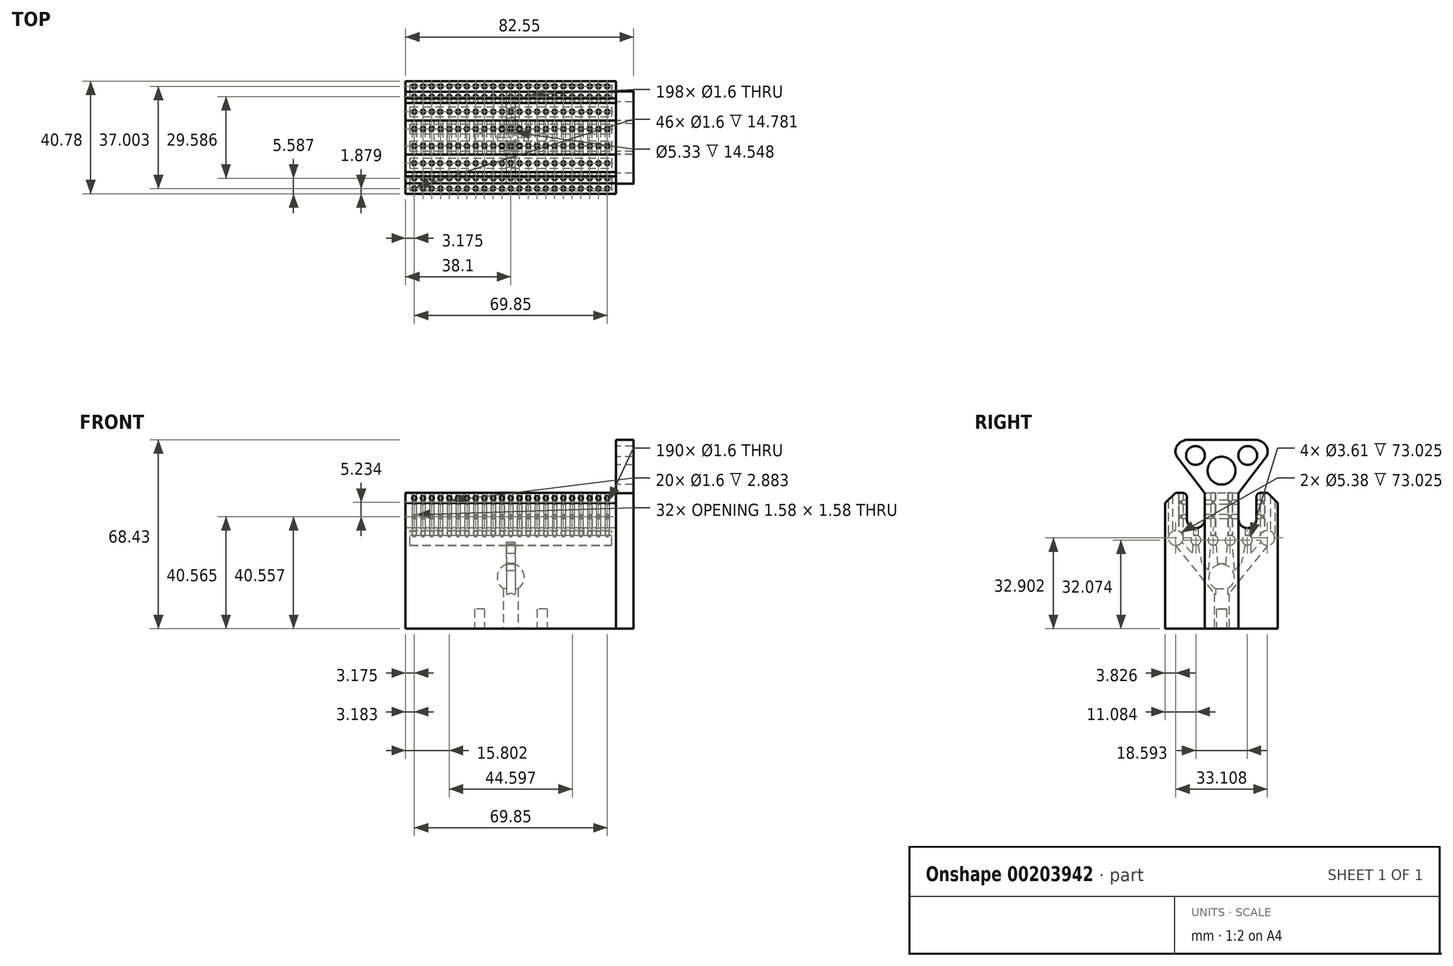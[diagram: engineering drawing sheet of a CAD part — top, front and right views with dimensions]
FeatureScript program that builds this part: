
annotation { "Feature Type Name" : "Feature", "Feature Type Description" : "" }
export const myFeature = defineFeature(function(context is Context, id is Id, definition is map)
    precondition{}
    {
        {
            var Q0;
            Q0=qCreatedBy(makeId("Top.planeOp"),FACE);
            var sketch = newSketch(context, id + "F0", { "sketchPlane" : qUnion([Q0])});
            skPoint(sketch, "E0.middle", {"position": v(0, 0) * mm});
            skCircle(sketch, "E1", {"center": v(-34.92, 18.5) * mm, "radius": 0.8 * mm});
            skCircle(sketch, "E2", {"center": v(-31.75, 18.5) * mm, "radius": 0.8 * mm});
            skCircle(sketch, "E3", {"center": v(-28.58, 18.5) * mm, "radius": 0.8 * mm});
            skCircle(sketch, "E4", {"center": v(-25.4, 18.5) * mm, "radius": 0.8 * mm});
            skCircle(sketch, "E5", {"center": v(-22.23, 18.5) * mm, "radius": 0.8 * mm});
            skCircle(sketch, "E6", {"center": v(-19.05, 18.5) * mm, "radius": 0.8 * mm});
            skCircle(sketch, "E7", {"center": v(-15.88, 18.5) * mm, "radius": 0.8 * mm});
            skCircle(sketch, "E8", {"center": v(-12.7, 18.5) * mm, "radius": 0.8 * mm});
            skCircle(sketch, "E9", {"center": v(-9.53, 18.5) * mm, "radius": 0.8 * mm});
            skCircle(sketch, "E10", {"center": v(-6.35, 18.5) * mm, "radius": 0.8 * mm});
            skCircle(sketch, "E11", {"center": v(-3.18, 18.5) * mm, "radius": 0.8 * mm});
            skCircle(sketch, "E12", {"center": v(-34.92, 9.3) * mm, "radius": 0.8 * mm});
            skCircle(sketch, "E13", {"center": v(-31.75, 9.33) * mm, "radius": 0.8 * mm});
            skCircle(sketch, "E14", {"center": v(-28.58, 9.33) * mm, "radius": 0.8 * mm});
            skCircle(sketch, "E15", {"center": v(-25.58, 9.3) * mm, "radius": 0.8 * mm});
            skCircle(sketch, "E16", {"center": v(-22.23, 9.33) * mm, "radius": 0.8 * mm});
            skCircle(sketch, "E17", {"center": v(-19.05, 9.33) * mm, "radius": 0.8 * mm});
            skCircle(sketch, "E18", {"center": v(-15.88, 9.33) * mm, "radius": 0.8 * mm});
            skCircle(sketch, "E19", {"center": v(-12.7, 9.33) * mm, "radius": 0.8 * mm});
            skCircle(sketch, "E20", {"center": v(-9.53, 9.33) * mm, "radius": 0.8 * mm});
            skCircle(sketch, "E21", {"center": v(-6.35, 9.33) * mm, "radius": 0.8 * mm});
            skCircle(sketch, "E22", {"center": v(-3.18, 9.33) * mm, "radius": 0.8 * mm});
            skCircle(sketch, "E23", {"center": v(0, 9.3) * mm, "radius": 0.8 * mm});
            skCircle(sketch, "E24", {"center": v(-34.92, 3.08) * mm, "radius": 0.8 * mm});
            skCircle(sketch, "E25", {"center": v(-31.75, 3.06) * mm, "radius": 0.8 * mm});
            skCircle(sketch, "E26", {"center": v(-28.62, 3.09) * mm, "radius": 0.8 * mm});
            skCircle(sketch, "E27", {"center": v(-25.4, 3.06) * mm, "radius": 0.8 * mm});
            skCircle(sketch, "E28", {"center": v(-22.23, 3.06) * mm, "radius": 0.8 * mm});
            skCircle(sketch, "E29", {"center": v(-19.05, 3.06) * mm, "radius": 0.8 * mm});
            skCircle(sketch, "E30", {"center": v(-15.88, 3.06) * mm, "radius": 0.8 * mm});
            skCircle(sketch, "E31", {"center": v(-12.7, 3.06) * mm, "radius": 0.8 * mm});
            skCircle(sketch, "E32", {"center": v(-9.53, 3.06) * mm, "radius": 0.8 * mm});
            skCircle(sketch, "E33", {"center": v(-6.35, 3.06) * mm, "radius": 0.8 * mm});
            skCircle(sketch, "E34", {"center": v(-3.18, 3.06) * mm, "radius": 0.88 * mm});
            skCircle(sketch, "E35", {"center": v(0, 3.18) * mm, "radius": 0.8 * mm});
            skCircle(sketch, "E36", {"center": v(-34.92, 14.73) * mm, "radius": 0.8 * mm});
            skCircle(sketch, "E37", {"center": v(-31.75, 14.73) * mm, "radius": 0.8 * mm});
            skCircle(sketch, "E38", {"center": v(-28.58, 14.73) * mm, "radius": 0.8 * mm});
            skCircle(sketch, "E39", {"center": v(-25.4, 14.73) * mm, "radius": 0.8 * mm});
            skCircle(sketch, "E40", {"center": v(-22.23, 14.73) * mm, "radius": 0.8 * mm});
            skCircle(sketch, "E41", {"center": v(-19.05, 14.73) * mm, "radius": 0.8 * mm});
            skCircle(sketch, "E42", {"center": v(-15.88, 14.73) * mm, "radius": 0.8 * mm});
            skCircle(sketch, "E43", {"center": v(-12.7, 14.73) * mm, "radius": 0.8 * mm});
            skCircle(sketch, "E44", {"center": v(-9.53, 14.73) * mm, "radius": 0.8 * mm});
            skCircle(sketch, "E45", {"center": v(-6.28, 14.8) * mm, "radius": 0.8 * mm});
            skCircle(sketch, "E46", {"center": v(-3.18, 14.73) * mm, "radius": 0.8 * mm});
            skCircle(sketch, "E47", {"center": v(0, 14.73) * mm, "radius": 0.8 * mm});
            skCircle(sketch, "E48.MirrorC", {"center": v(0, -3.18) * mm, "radius": 0.8 * mm});
            skCircle(sketch, "E49.MirrorC", {"center": v(-3.18, -3.06) * mm, "radius": 0.88 * mm});
            skCircle(sketch, "E50.MirrorC", {"center": v(-6.35, -3.06) * mm, "radius": 0.8 * mm});
            skCircle(sketch, "E51.MirrorC", {"center": v(-9.53, -3.06) * mm, "radius": 0.8 * mm});
            skCircle(sketch, "E52.MirrorC", {"center": v(-12.7, -3.06) * mm, "radius": 0.8 * mm});
            skCircle(sketch, "E53.MirrorC", {"center": v(-15.88, -3.06) * mm, "radius": 0.8 * mm});
            skCircle(sketch, "E54.MirrorC", {"center": v(-19.05, -3.06) * mm, "radius": 0.8 * mm});
            skCircle(sketch, "E55.MirrorC", {"center": v(-22.23, -3.06) * mm, "radius": 0.8 * mm});
            skCircle(sketch, "E56.MirrorC", {"center": v(-25.4, -3.06) * mm, "radius": 0.8 * mm});
            skCircle(sketch, "E57.MirrorC", {"center": v(-28.62, -3.09) * mm, "radius": 0.8 * mm});
            skCircle(sketch, "E58.MirrorC", {"center": v(-31.75, -3.06) * mm, "radius": 0.8 * mm});
            skCircle(sketch, "E59.MirrorC", {"center": v(-34.92, -3.08) * mm, "radius": 0.8 * mm});
            skCircle(sketch, "E60.MirrorC", {"center": v(-34.92, -9.3) * mm, "radius": 0.8 * mm});
            skCircle(sketch, "E61.MirrorC", {"center": v(-31.75, -9.33) * mm, "radius": 0.8 * mm});
            skCircle(sketch, "E62.MirrorC", {"center": v(-28.58, -9.33) * mm, "radius": 0.8 * mm});
            skCircle(sketch, "E63.MirrorC", {"center": v(-25.58, -9.3) * mm, "radius": 0.8 * mm});
            skCircle(sketch, "E64.MirrorC", {"center": v(-22.23, -9.33) * mm, "radius": 0.8 * mm});
            skCircle(sketch, "E65.MirrorC", {"center": v(-19.05, -9.33) * mm, "radius": 0.8 * mm});
            skCircle(sketch, "E66.MirrorC", {"center": v(-15.88, -9.33) * mm, "radius": 0.8 * mm});
            skCircle(sketch, "E67.MirrorC", {"center": v(-12.7, -9.33) * mm, "radius": 0.8 * mm});
            skCircle(sketch, "E68.MirrorC", {"center": v(-9.53, -9.33) * mm, "radius": 0.8 * mm});
            skCircle(sketch, "E69.MirrorC", {"center": v(-6.35, -9.33) * mm, "radius": 0.8 * mm});
            skCircle(sketch, "E70.MirrorC", {"center": v(-3.18, -9.33) * mm, "radius": 0.8 * mm});
            skCircle(sketch, "E71.MirrorC", {"center": v(0, -9.3) * mm, "radius": 0.8 * mm});
            skCircle(sketch, "E72.MirrorC", {"center": v(0, -18.5) * mm, "radius": 0.8 * mm});
            skCircle(sketch, "E73.MirrorC", {"center": v(-3.18, -14.73) * mm, "radius": 0.8 * mm});
            skCircle(sketch, "E74.MirrorC", {"center": v(-3.18, -18.5) * mm, "radius": 0.8 * mm});
            skCircle(sketch, "E75.MirrorC", {"center": v(-6.35, -18.5) * mm, "radius": 0.8 * mm});
            skCircle(sketch, "E76.MirrorC", {"center": v(-6.28, -14.8) * mm, "radius": 0.8 * mm});
            skCircle(sketch, "E77.MirrorC", {"center": v(-9.53, -14.73) * mm, "radius": 0.8 * mm});
            skCircle(sketch, "E78.MirrorC", {"center": v(-9.53, -18.5) * mm, "radius": 0.8 * mm});
            skCircle(sketch, "E79.MirrorC", {"center": v(-12.7, -14.73) * mm, "radius": 0.8 * mm});
            skCircle(sketch, "E80.MirrorC", {"center": v(-12.7, -18.5) * mm, "radius": 0.8 * mm});
            skCircle(sketch, "E81.MirrorC", {"center": v(-15.88, -14.73) * mm, "radius": 0.8 * mm});
            skCircle(sketch, "E82.MirrorC", {"center": v(-15.88, -18.5) * mm, "radius": 0.8 * mm});
            skCircle(sketch, "E83.MirrorC", {"center": v(-19.05, -18.5) * mm, "radius": 0.8 * mm});
            skCircle(sketch, "E84.MirrorC", {"center": v(-19.05, -14.73) * mm, "radius": 0.8 * mm});
            skCircle(sketch, "E85.MirrorC", {"center": v(-22.23, -14.73) * mm, "radius": 0.8 * mm});
            skCircle(sketch, "E86.MirrorC", {"center": v(-22.23, -18.5) * mm, "radius": 0.8 * mm});
            skCircle(sketch, "E87.MirrorC", {"center": v(-25.4, -18.5) * mm, "radius": 0.8 * mm});
            skCircle(sketch, "E88.MirrorC", {"center": v(-25.4, -14.73) * mm, "radius": 0.8 * mm});
            skCircle(sketch, "E89.MirrorC", {"center": v(-28.58, -14.73) * mm, "radius": 0.8 * mm});
            skCircle(sketch, "E90.MirrorC", {"center": v(-28.58, -18.5) * mm, "radius": 0.8 * mm});
            skCircle(sketch, "E91.MirrorC", {"center": v(-34.92, -14.73) * mm, "radius": 0.8 * mm});
            skCircle(sketch, "E92.MirrorC", {"center": v(-31.75, -14.73) * mm, "radius": 0.8 * mm});
            skCircle(sketch, "E93.MirrorC", {"center": v(-31.75, -18.5) * mm, "radius": 0.8 * mm});
            skCircle(sketch, "E94.MirrorC", {"center": v(-34.92, -18.5) * mm, "radius": 0.8 * mm});
            skCircle(sketch, "E95.MirrorC", {"center": v(6.28, 14.8) * mm, "radius": 0.8 * mm});
            skCircle(sketch, "E96.MirrorC", {"center": v(6.35, 18.5) * mm, "radius": 0.8 * mm});
            skCircle(sketch, "E97.MirrorC", {"center": v(22.23, 18.5) * mm, "radius": 0.8 * mm});
            skCircle(sketch, "E98.MirrorC", {"center": v(31.75, 14.73) * mm, "radius": 0.8 * mm});
            skCircle(sketch, "E99.MirrorC", {"center": v(9.53, 14.73) * mm, "radius": 0.8 * mm});
            skCircle(sketch, "E100.MirrorC", {"center": v(0, 18.5) * mm, "radius": 0.8 * mm});
            skCircle(sketch, "E101.MirrorC", {"center": v(12.7, 18.5) * mm, "radius": 0.8 * mm});
            skCircle(sketch, "E102.MirrorC", {"center": v(3.18, 14.73) * mm, "radius": 0.8 * mm});
            skCircle(sketch, "E103.MirrorC", {"center": v(22.23, 14.73) * mm, "radius": 0.8 * mm});
            skCircle(sketch, "E104.MirrorC", {"center": v(34.92, 18.5) * mm, "radius": 0.8 * mm});
            skCircle(sketch, "E105.MirrorC", {"center": v(19.05, 18.5) * mm, "radius": 0.8 * mm});
            skCircle(sketch, "E106.MirrorC", {"center": v(25.4, 18.5) * mm, "radius": 0.8 * mm});
            skCircle(sketch, "E107.MirrorC", {"center": v(12.7, 14.73) * mm, "radius": 0.8 * mm});
            skCircle(sketch, "E108.MirrorC", {"center": v(15.88, 14.73) * mm, "radius": 0.8 * mm});
            skCircle(sketch, "E109.MirrorC", {"center": v(9.53, 18.5) * mm, "radius": 0.8 * mm});
            skCircle(sketch, "E110.MirrorC", {"center": v(28.58, 18.5) * mm, "radius": 0.8 * mm});
            skCircle(sketch, "E111.MirrorC", {"center": v(3.18, 18.5) * mm, "radius": 0.8 * mm});
            skCircle(sketch, "E112.MirrorC", {"center": v(31.75, 18.5) * mm, "radius": 0.8 * mm});
            skCircle(sketch, "E113.MirrorC", {"center": v(19.05, 14.73) * mm, "radius": 0.8 * mm});
            skCircle(sketch, "E114.MirrorC", {"center": v(15.88, 18.5) * mm, "radius": 0.8 * mm});
            skCircle(sketch, "E115.MirrorC", {"center": v(28.58, 14.73) * mm, "radius": 0.8 * mm});
            skCircle(sketch, "E116.MirrorC", {"center": v(25.4, 14.73) * mm, "radius": 0.8 * mm});
            skCircle(sketch, "E117.MirrorC", {"center": v(22.23, 9.33) * mm, "radius": 0.8 * mm});
            skCircle(sketch, "E118.MirrorC", {"center": v(12.7, 9.33) * mm, "radius": 0.8 * mm});
            skCircle(sketch, "E119.MirrorC", {"center": v(6.35, 9.33) * mm, "radius": 0.8 * mm});
            skCircle(sketch, "E120.MirrorC", {"center": v(28.58, 9.33) * mm, "radius": 0.8 * mm});
            skCircle(sketch, "E121.MirrorC", {"center": v(34.92, 9.3) * mm, "radius": 0.8 * mm});
            skCircle(sketch, "E122.MirrorC", {"center": v(25.58, 9.3) * mm, "radius": 0.8 * mm});
            skCircle(sketch, "E123.MirrorC", {"center": v(15.88, 9.33) * mm, "radius": 0.8 * mm});
            skCircle(sketch, "E124.MirrorC", {"center": v(9.53, 9.33) * mm, "radius": 0.8 * mm});
            skCircle(sketch, "E125.MirrorC", {"center": v(31.75, 9.33) * mm, "radius": 0.8 * mm});
            skCircle(sketch, "E126.MirrorC", {"center": v(19.05, 9.33) * mm, "radius": 0.8 * mm});
            skCircle(sketch, "E127.MirrorC", {"center": v(3.18, 9.33) * mm, "radius": 0.8 * mm});
            skCircle(sketch, "E128.MirrorC", {"center": v(9.53, 3.06) * mm, "radius": 0.8 * mm});
            skCircle(sketch, "E129.MirrorC", {"center": v(12.7, 3.06) * mm, "radius": 0.8 * mm});
            skCircle(sketch, "E130.MirrorC", {"center": v(22.23, 3.06) * mm, "radius": 0.8 * mm});
            skCircle(sketch, "E131.MirrorC", {"center": v(6.35, 3.06) * mm, "radius": 0.8 * mm});
            skCircle(sketch, "E132.MirrorC", {"center": v(31.75, 3.06) * mm, "radius": 0.8 * mm});
            skCircle(sketch, "E133.MirrorC", {"center": v(3.18, 3.06) * mm, "radius": 0.88 * mm});
            skCircle(sketch, "E134.MirrorC", {"center": v(15.88, 3.06) * mm, "radius": 0.8 * mm});
            skCircle(sketch, "E135.MirrorC", {"center": v(19.05, 3.06) * mm, "radius": 0.8 * mm});
            skCircle(sketch, "E136.MirrorC", {"center": v(28.62, 3.09) * mm, "radius": 0.8 * mm});
            skCircle(sketch, "E137.MirrorC", {"center": v(25.4, 3.06) * mm, "radius": 0.8 * mm});
            skCircle(sketch, "E138.MirrorC", {"center": v(34.92, 3.08) * mm, "radius": 0.8 * mm});
            skCircle(sketch, "E139.MirrorC", {"center": v(28.62, -3.09) * mm, "radius": 0.8 * mm});
            skCircle(sketch, "E140.MirrorC", {"center": v(12.7, -3.06) * mm, "radius": 0.8 * mm});
            skCircle(sketch, "E141.MirrorC", {"center": v(34.92, -3.08) * mm, "radius": 0.8 * mm});
            skCircle(sketch, "E142.MirrorC", {"center": v(9.53, -3.06) * mm, "radius": 0.8 * mm});
            skCircle(sketch, "E143.MirrorC", {"center": v(22.23, -3.06) * mm, "radius": 0.8 * mm});
            skCircle(sketch, "E144.MirrorC", {"center": v(31.75, -3.06) * mm, "radius": 0.8 * mm});
            skCircle(sketch, "E145.MirrorC", {"center": v(6.35, -3.06) * mm, "radius": 0.8 * mm});
            skCircle(sketch, "E146.MirrorC", {"center": v(15.88, -3.06) * mm, "radius": 0.8 * mm});
            skCircle(sketch, "E147.MirrorC", {"center": v(19.05, -3.06) * mm, "radius": 0.8 * mm});
            skCircle(sketch, "E148.MirrorC", {"center": v(25.4, -3.06) * mm, "radius": 0.8 * mm});
            skCircle(sketch, "E149.MirrorC", {"center": v(3.18, -3.06) * mm, "radius": 0.88 * mm});
            skCircle(sketch, "E150.MirrorC", {"center": v(12.7, -9.33) * mm, "radius": 0.8 * mm});
            skCircle(sketch, "E151.MirrorC", {"center": v(9.53, -9.33) * mm, "radius": 0.8 * mm});
            skCircle(sketch, "E152.MirrorC", {"center": v(34.92, -9.3) * mm, "radius": 0.8 * mm});
            skCircle(sketch, "E153.MirrorC", {"center": v(6.35, -9.33) * mm, "radius": 0.8 * mm});
            skCircle(sketch, "E154.MirrorC", {"center": v(22.23, -9.33) * mm, "radius": 0.8 * mm});
            skCircle(sketch, "E155.MirrorC", {"center": v(3.18, -9.33) * mm, "radius": 0.8 * mm});
            skCircle(sketch, "E156.MirrorC", {"center": v(28.58, -9.33) * mm, "radius": 0.8 * mm});
            skCircle(sketch, "E157.MirrorC", {"center": v(15.88, -9.33) * mm, "radius": 0.8 * mm});
            skCircle(sketch, "E158.MirrorC", {"center": v(31.75, -9.33) * mm, "radius": 0.8 * mm});
            skCircle(sketch, "E159.MirrorC", {"center": v(19.05, -9.33) * mm, "radius": 0.8 * mm});
            skCircle(sketch, "E160.MirrorC", {"center": v(25.58, -9.3) * mm, "radius": 0.8 * mm});
            skCircle(sketch, "E161.MirrorC", {"center": v(25.4, -18.5) * mm, "radius": 0.8 * mm});
            skCircle(sketch, "E162.MirrorC", {"center": v(0, -14.73) * mm, "radius": 0.8 * mm});
            skCircle(sketch, "E163.MirrorC", {"center": v(6.28, -14.8) * mm, "radius": 0.8 * mm});
            skCircle(sketch, "E164.MirrorC", {"center": v(15.88, -18.5) * mm, "radius": 0.8 * mm});
            skCircle(sketch, "E165.MirrorC", {"center": v(9.53, -18.5) * mm, "radius": 0.8 * mm});
            skCircle(sketch, "E166.MirrorC", {"center": v(34.92, -18.5) * mm, "radius": 0.8 * mm});
            skCircle(sketch, "E167.MirrorC", {"center": v(34.92, -14.73) * mm, "radius": 0.8 * mm});
            skCircle(sketch, "E168.MirrorC", {"center": v(6.35, -18.5) * mm, "radius": 0.8 * mm});
            skCircle(sketch, "E169.MirrorC", {"center": v(12.7, -18.5) * mm, "radius": 0.8 * mm});
            skCircle(sketch, "E170.MirrorC", {"center": v(19.05, -14.73) * mm, "radius": 0.8 * mm});
            skCircle(sketch, "E171.MirrorC", {"center": v(3.18, -14.73) * mm, "radius": 0.8 * mm});
            skCircle(sketch, "E172.MirrorC", {"center": v(31.75, -18.5) * mm, "radius": 0.8 * mm});
            skCircle(sketch, "E173.MirrorC", {"center": v(12.7, -14.73) * mm, "radius": 0.8 * mm});
            skCircle(sketch, "E174.MirrorC", {"center": v(15.88, -14.73) * mm, "radius": 0.8 * mm});
            skCircle(sketch, "E175.MirrorC", {"center": v(31.75, -14.73) * mm, "radius": 0.8 * mm});
            skCircle(sketch, "E176.MirrorC", {"center": v(9.53, -14.73) * mm, "radius": 0.8 * mm});
            skCircle(sketch, "E177.MirrorC", {"center": v(3.18, -18.5) * mm, "radius": 0.8 * mm});
            skCircle(sketch, "E178.MirrorC", {"center": v(22.23, -14.73) * mm, "radius": 0.8 * mm});
            skCircle(sketch, "E179.MirrorC", {"center": v(19.05, -18.5) * mm, "radius": 0.8 * mm});
            skCircle(sketch, "E180.MirrorC", {"center": v(25.4, -14.73) * mm, "radius": 0.8 * mm});
            skCircle(sketch, "E181.MirrorC", {"center": v(28.58, -14.73) * mm, "radius": 0.8 * mm});
            skCircle(sketch, "E182.MirrorC", {"center": v(22.23, -18.5) * mm, "radius": 0.8 * mm});
            skCircle(sketch, "E183.MirrorC", {"center": v(28.58, -18.5) * mm, "radius": 0.8 * mm});
            skCircle(sketch, "E184.MirrorC", {"center": v(34.92, 14.73) * mm, "radius": 0.8 * mm});
            skSolve(sketch);
        }
        {
            var Q0;
            Q0=qCreatedBy(makeId("Right.planeOp"),FACE);
            var sketch = newSketch(context, id + "F1", { "sketchPlane" : qUnion([Q0])});
            skArc(sketch, "E185", {"start": v(6.12, 39.66) * mm, "mid": v(9.33, 36.45) * mm, "end": v(12.55, 39.66) * mm});
            skLineSegment(sketch, "E186", {"start": v(12.55, 39.66) * mm, "end": v(12.55, 47.59) * mm});
            skArc(sketch, "E187", {"start": v(12.55, 47.59) * mm, "mid": v(13, 48.7) * mm, "end": v(14.1, 49.19) * mm});
            skLineSegment(sketch, "E188", {"start": v(14.1, 49.19) * mm, "end": v(16.62, 49.19) * mm});
            skLineSegment(sketch, "E189", {"start": v(20.38, 39.66) * mm, "end": v(20.38, 45.48) * mm});
            skLineSegment(sketch, "E190", {"start": v(16.62, 49.19) * mm, "end": v(20.38, 45.48) * mm});
            skLineSegment(sketch, "E191", {"start": v(6.12, 49.19) * mm, "end": v(6.12, 39.66) * mm});
            skLineSegment(sketch, "E192.MirrorCS", {"start": v(-6.12, 49.19) * mm, "end": v(-6.12, 39.66) * mm});
            skArc(sketch, "E193.MirrorCS", {"start": v(-6.12, 39.66) * mm, "mid": v(-9.33, 36.45) * mm, "end": v(-12.55, 39.66) * mm});
            skLineSegment(sketch, "E194.MirrorCS", {"start": v(-12.55, 39.66) * mm, "end": v(-12.55, 47.59) * mm});
            skArc(sketch, "E195.MirrorCS", {"start": v(-12.55, 47.59) * mm, "mid": v(-13, 48.7) * mm, "end": v(-14.1, 49.19) * mm});
            skLineSegment(sketch, "E196.MirrorCS", {"start": v(-14.1, 49.19) * mm, "end": v(-16.62, 49.19) * mm});
            skLineSegment(sketch, "E197.MirrorCS", {"start": v(-16.62, 49.19) * mm, "end": v(-20.38, 45.48) * mm});
            skLineSegment(sketch, "E198.MirrorCS", {"start": v(-20.38, 39.66) * mm, "end": v(-20.38, 45.48) * mm});
            skLineSegment(sketch, "E199", {"start": v(-20.38, 39.66) * mm, "end": v(-20.38, 0) * mm});
            skLineSegment(sketch, "E200", {"start": v(20.4, 0) * mm, "end": v(20.38, 39.66) * mm});
            skLineSegment(sketch, "E201", {"start": v(-6.12, 49.19) * mm, "end": v(6.12, 49.19) * mm});
            skLineSegment(sketch, "E202", {"start": v(-20.38, 0) * mm, "end": v(20.4, 0) * mm});
            skSolve(sketch);
        }
        {
            var Q0;
            Q0=qCreatedBy(makeId("Right.planeOp"),FACE);
            var sketch = newSketch(context, id + "F2", { "sketchPlane" : qUnion([Q0])});
            skLineSegment(sketch, "E203", {"start": v(0, 0) * mm, "end": v(-6.13, 0) * mm});
            skLineSegment(sketch, "E204", {"start": v(-6.13, 0) * mm, "end": v(-6.13, 49.13) * mm});
            skLineSegment(sketch, "E205", {"start": v(-6.13, 49.13) * mm, "end": v(-17.04, 63.34) * mm});
            skLineSegment(sketch, "E206", {"start": v(-17.04, 63.34) * mm, "end": v(-17.04, 68.43) * mm});
            skLineSegment(sketch, "E207.MirrorCS", {"start": v(0, 0) * mm, "end": v(6.13, 0) * mm});
            skLineSegment(sketch, "E208.MirrorCS", {"start": v(6.13, 0) * mm, "end": v(6.13, 49.13) * mm});
            skLineSegment(sketch, "E209.MirrorCS", {"start": v(6.13, 49.13) * mm, "end": v(17.04, 63.34) * mm});
            skLineSegment(sketch, "E210.MirrorCS", {"start": v(17.04, 63.34) * mm, "end": v(17.04, 68.43) * mm});
            skLineSegment(sketch, "E211", {"start": v(-17.04, 68.43) * mm, "end": v(17.04, 68.43) * mm});
            skCircle(sketch, "E212", {"center": v(0, 57.25) * mm, "radius": 5.04 * mm});
            skCircle(sketch, "E213", {"center": v(9.44, 62.75) * mm, "radius": 3.4 * mm});
            skCircle(sketch, "E214.MirrorC", {"center": v(-9.44, 62.75) * mm, "radius": 3.4 * mm});
            skSolve(sketch);
        }
        {
            var Q0;
            Q0=qCreatedBy(makeId("Front.planeOp"),FACE);
            var sketch = newSketch(context, id + "F3", { "sketchPlane" : qUnion([Q0])});
            skCircle(sketch, "E215", {"center": v(-34.93, 45.8) * mm, "radius": 0.8 * mm});
            skCircle(sketch, "E216", {"center": v(-31.75, 45.8) * mm, "radius": 0.8 * mm});
            skCircle(sketch, "E217", {"center": v(-28.58, 45.8) * mm, "radius": 0.8 * mm});
            skCircle(sketch, "E218", {"center": v(-25.4, 45.8) * mm, "radius": 0.8 * mm});
            skCircle(sketch, "E219", {"center": v(-22.3, 45.8) * mm, "radius": 0.8 * mm});
            skCircle(sketch, "E220", {"center": v(-19.05, 45.8) * mm, "radius": 0.8 * mm});
            skCircle(sketch, "E221", {"center": v(-15.79, 45.8) * mm, "radius": 0.8 * mm});
            skCircle(sketch, "E222", {"center": v(-12.7, 45.8) * mm, "radius": 0.8 * mm});
            skCircle(sketch, "E223", {"center": v(-6.35, 45.8) * mm, "radius": 0.8 * mm});
            skCircle(sketch, "E224", {"center": v(-9.53, 45.8) * mm, "radius": 0.8 * mm});
            skCircle(sketch, "E225", {"center": v(-3.18, 45.8) * mm, "radius": 0.8 * mm});
            skCircle(sketch, "E226", {"center": v(0, 45.8) * mm, "radius": 0.8 * mm});
            skCircle(sketch, "E227", {"center": v(0, 40.56) * mm, "radius": 0.8 * mm});
            skCircle(sketch, "E228", {"center": v(-3.18, 40.56) * mm, "radius": 0.8 * mm});
            skCircle(sketch, "E229", {"center": v(-6.35, 40.56) * mm, "radius": 0.8 * mm});
            skCircle(sketch, "E230", {"center": v(-9.53, 40.56) * mm, "radius": 0.8 * mm});
            skCircle(sketch, "E231", {"center": v(-12.7, 40.56) * mm, "radius": 0.8 * mm});
            skCircle(sketch, "E232", {"center": v(-15.79, 40.56) * mm, "radius": 0.8 * mm});
            skCircle(sketch, "E233", {"center": v(-19.05, 40.56) * mm, "radius": 0.8 * mm});
            skCircle(sketch, "E234", {"center": v(-22.23, 40.56) * mm, "radius": 0.8 * mm});
            skCircle(sketch, "E235", {"center": v(-25.4, 40.56) * mm, "radius": 0.8 * mm});
            skCircle(sketch, "E236", {"center": v(-28.58, 40.56) * mm, "radius": 0.8 * mm});
            skCircle(sketch, "E237", {"center": v(-31.75, 40.56) * mm, "radius": 0.8 * mm});
            skCircle(sketch, "E238", {"center": v(-34.93, 40.56) * mm, "radius": 0.8 * mm});
            skCircle(sketch, "E239.MirrorC", {"center": v(22.23, 40.56) * mm, "radius": 0.8 * mm});
            skCircle(sketch, "E240.MirrorC", {"center": v(19.05, 40.56) * mm, "radius": 0.8 * mm});
            skCircle(sketch, "E241.MirrorC", {"center": v(25.4, 40.56) * mm, "radius": 0.8 * mm});
            skCircle(sketch, "E242.MirrorC", {"center": v(9.53, 45.8) * mm, "radius": 0.8 * mm});
            skCircle(sketch, "E243.MirrorC", {"center": v(6.35, 45.8) * mm, "radius": 0.8 * mm});
            skCircle(sketch, "E244.MirrorC", {"center": v(3.18, 45.8) * mm, "radius": 0.8 * mm});
            skCircle(sketch, "E245.MirrorC", {"center": v(31.75, 40.56) * mm, "radius": 0.8 * mm});
            skCircle(sketch, "E246.MirrorC", {"center": v(12.7, 40.56) * mm, "radius": 0.8 * mm});
            skCircle(sketch, "E247.MirrorC", {"center": v(34.93, 45.8) * mm, "radius": 0.8 * mm});
            skCircle(sketch, "E248.MirrorC", {"center": v(3.18, 40.56) * mm, "radius": 0.8 * mm});
            skCircle(sketch, "E249.MirrorC", {"center": v(19.05, 45.8) * mm, "radius": 0.8 * mm});
            skCircle(sketch, "E250.MirrorC", {"center": v(25.4, 45.8) * mm, "radius": 0.8 * mm});
            skCircle(sketch, "E251.MirrorC", {"center": v(6.35, 40.56) * mm, "radius": 0.8 * mm});
            skCircle(sketch, "E252.MirrorC", {"center": v(34.93, 40.56) * mm, "radius": 0.8 * mm});
            skCircle(sketch, "E253.MirrorC", {"center": v(15.79, 40.56) * mm, "radius": 0.8 * mm});
            skCircle(sketch, "E254.MirrorC", {"center": v(15.79, 45.8) * mm, "radius": 0.8 * mm});
            skCircle(sketch, "E255.MirrorC", {"center": v(12.7, 45.8) * mm, "radius": 0.8 * mm});
            skCircle(sketch, "E256.MirrorC", {"center": v(22.3, 45.8) * mm, "radius": 0.8 * mm});
            skCircle(sketch, "E257.MirrorC", {"center": v(31.75, 45.8) * mm, "radius": 0.8 * mm});
            skCircle(sketch, "E258.MirrorC", {"center": v(28.58, 45.8) * mm, "radius": 0.8 * mm});
            skCircle(sketch, "E259.MirrorC", {"center": v(9.53, 40.56) * mm, "radius": 0.8 * mm});
            skCircle(sketch, "E260.MirrorC", {"center": v(28.58, 40.56) * mm, "radius": 0.8 * mm});
            skSolve(sketch);
        }
        {
            var Q0;
            Q0=qCreatedBy(makeId("Right.planeOp"),FACE);
            var sketch = newSketch(context, id + "F4", { "sketchPlane" : qUnion([Q0])});
            skCircle(sketch, "E261", {"center": v(-9.3, 32.07) * mm, "radius": 1.8 * mm});
            skCircle(sketch, "E262", {"center": v(-16.55, 32.9) * mm, "radius": 2.7 * mm});
            skCircle(sketch, "E263.MirrorC", {"center": v(16.55, 32.9) * mm, "radius": 2.7 * mm});
            skCircle(sketch, "E264", {"center": v(-3.07, 32.07) * mm, "radius": 1.8 * mm});
            skCircle(sketch, "E265.MirrorC", {"center": v(3.07, 32.07) * mm, "radius": 1.8 * mm});
            skCircle(sketch, "E266.MirrorC", {"center": v(9.3, 32.07) * mm, "radius": 1.8 * mm});
            skSolve(sketch);
        }
        {
            var Q0;
            Q0=qCreatedBy(makeId("Top.planeOp"),FACE);
            var sketch = newSketch(context, id + "F5", { "sketchPlane" : qUnion([Q0])});
            skCircle(sketch, "E267", {"center": v(0, 0) * mm, "radius": 2.67 * mm});
            skCircle(sketch, "E268", {"center": v(-11.3, 0) * mm, "radius": 1.83 * mm});
            skCircle(sketch, "E269", {"center": v(11.3, 0) * mm, "radius": 1.83 * mm});
            skSolve(sketch);
        }
        {
            var Q0;
            Q0=qCreatedBy(makeId("Right.planeOp"),FACE);
            var sketch = newSketch(context, id + "F6", { "sketchPlane" : qUnion([Q0])});
            skLineSegment(sketch, "E270", {"start": v(0, 18.65) * mm, "end": v(7.4, 18.65) * mm});
            skLineSegment(sketch, "E271", {"start": v(7.4, 18.65) * mm, "end": v(0, 18.65) * mm});
            skLineSegment(sketch, "E272", {"start": v(-7.68, 18.65) * mm, "end": v(0, 18.65) * mm});
            skArc(sketch, "E273", {"start": v(4.9, 18.65) * mm, "mid": v(0, 23.55) * mm, "end": v(-4.9, 18.65) * mm});
            skLineSegment(sketch, "E274", {"start": v(-7.68, 18.65) * mm, "end": v(7.4, 18.65) * mm});
            skSolve(sketch);
        }
        {
            var Q0;
            Q0=qCreatedBy(makeId("Right.planeOp"),FACE);
            var sketch = newSketch(context, id + "F7", { "sketchPlane" : qUnion([Q0])});
            skLineSegment(sketch, "E275", {"start": v(-2.1, 32) * mm, "end": v(-1.47, 23.24) * mm});
            skLineSegment(sketch, "E276", {"start": v(-16.53, 32) * mm, "end": v(-14.93, 32) * mm});
            skLineSegment(sketch, "E277", {"start": v(-16.53, 32) * mm, "end": v(-18.13, 32) * mm});
            skLineSegment(sketch, "E278", {"start": v(-10.57, 32) * mm, "end": v(-10.57, 27.36) * mm});
            skLineSegment(sketch, "E279", {"start": v(-8.83, 32) * mm, "end": v(-7.18, 23.76) * mm});
            skLineSegment(sketch, "E280", {"start": v(-4.7, 21.13) * mm, "end": v(-7.18, 23.76) * mm});
            skLineSegment(sketch, "E281", {"start": v(-18.13, 32) * mm, "end": v(-2.45, 12.5) * mm});
            skLineSegment(sketch, "E282", {"start": v(-4.7, 21.13) * mm, "end": v(-3.83, 32) * mm});
            skLineSegment(sketch, "E283", {"start": v(-10.57, 32) * mm, "end": v(-8.83, 32) * mm});
            skLineSegment(sketch, "E284.trimOffspring", {"start": v(-3.83, 32) * mm, "end": v(-2.1, 32) * mm});
            skLineSegment(sketch, "E285.trimOffspring", {"start": v(-10.57, 27.36) * mm, "end": v(-14.93, 32) * mm});
            skLineSegment(sketch, "E286", {"start": v(-1.47, 23.24) * mm, "end": v(0, 23.24) * mm});
            skLineSegment(sketch, "E287", {"start": v(-2.45, 12.5) * mm, "end": v(0, 12.5) * mm});
            skLineSegment(sketch, "E288.MirrorCS", {"start": v(10.57, 27.36) * mm, "end": v(14.93, 32) * mm});
            skLineSegment(sketch, "E289.MirrorCS", {"start": v(8.83, 32) * mm, "end": v(7.18, 23.76) * mm});
            skLineSegment(sketch, "E290.MirrorCS", {"start": v(4.7, 21.13) * mm, "end": v(3.83, 32) * mm});
            skLineSegment(sketch, "E291.MirrorCS", {"start": v(4.7, 21.13) * mm, "end": v(7.18, 23.76) * mm});
            skLineSegment(sketch, "E292.MirrorCS", {"start": v(2.1, 32) * mm, "end": v(1.47, 23.24) * mm});
            skLineSegment(sketch, "E293.MirrorCS", {"start": v(2.45, 12.5) * mm, "end": v(0, 12.5) * mm});
            skLineSegment(sketch, "E294.MirrorCS", {"start": v(16.53, 32) * mm, "end": v(18.13, 32) * mm});
            skLineSegment(sketch, "E295.MirrorCS", {"start": v(1.47, 23.24) * mm, "end": v(0, 23.24) * mm});
            skLineSegment(sketch, "E296.MirrorCS", {"start": v(16.53, 32) * mm, "end": v(14.93, 32) * mm});
            skLineSegment(sketch, "E297.MirrorCS", {"start": v(3.83, 32) * mm, "end": v(2.1, 32) * mm});
            skLineSegment(sketch, "E298.MirrorCS", {"start": v(18.13, 32) * mm, "end": v(2.45, 12.5) * mm});
            skLineSegment(sketch, "E299.MirrorCS", {"start": v(10.57, 32) * mm, "end": v(10.57, 27.36) * mm});
            skLineSegment(sketch, "E300.MirrorCS", {"start": v(10.57, 32) * mm, "end": v(8.83, 32) * mm});
            skSolve(sketch);
        }
        {
            var Q0;
            Q0=makeQuery(id+"F1.imprint","IMPRINT",FACE,{"disambiguationData":[TD([[makeQuery(id+"F1.imprint","IMPRINT",EDGE,{"derivedFrom":sQuery(id+"F1.wireOp",EDGE,"E185")}),-1.0]])]});
            extrude(context, id + "F8", {"entities" : qUnion([Q0]), "endBound" : BoundingType.SYMMETRIC, "depth" : 76.2 * mm});
        }
        {
            var Q0;
            Q0 = qSketchRegion(id + "F4", true);
            extrude(context, id + "F9", {"entities" : qUnion([Q0]), "operationType" : NewBodyOperationType.REMOVE, "endBound" : BoundingType.SYMMETRIC, "oppositeDirection" : true, "depth" : 73.02 * mm});
        }
        {
            var Q0;
            Q0 = qSketchRegion(id + "F0", true);
            var Q1;
            Q1=makeQuery(id+"F8.opExtrude","SWEPT_FACE",FACE,{"disambiguationData":[OSD([sQuery(id+"F1.wireOp",EDGE,"E201")])]});
            extrude(context, id + "F10", {"entities" : qUnion([Q0]), "operationType" : NewBodyOperationType.REMOVE, "endBound" : BoundingType.THROUGH_ALL, "endBoundEntityFace" : qUnion([Q1]), "depth" : 49.19 * mm, "hasSecondDirection" : true, "secondDirectionOppositeDirection" : false, "secondDirectionDepth" : 33.35 * mm});
        }
        {
            var Q0;
            Q0 = qSketchRegion(id + "F2", true);
            var Q1;
            Q1=makeQuery(id+"F8.opExtrude","CAP_FACE",FACE,{"disambiguationData":[OSD([sQuery(id+"F1.wireOp",EDGE,"E185"),sQuery(id+"F1.wireOp",EDGE,"E186"),sQuery(id+"F1.wireOp",EDGE,"E187"),sQuery(id+"F1.wireOp",EDGE,"E188"),sQuery(id+"F1.wireOp",EDGE,"E189"),sQuery(id+"F1.wireOp",EDGE,"E190"),sQuery(id+"F1.wireOp",EDGE,"E191"),sQuery(id+"F1.wireOp",EDGE,"E192.MirrorCS"),sQuery(id+"F1.wireOp",EDGE,"E193.MirrorCS"),sQuery(id+"F1.wireOp",EDGE,"E194.MirrorCS"),sQuery(id+"F1.wireOp",EDGE,"E195.MirrorCS"),sQuery(id+"F1.wireOp",EDGE,"E196.MirrorCS"),sQuery(id+"F1.wireOp",EDGE,"E197.MirrorCS"),sQuery(id+"F1.wireOp",EDGE,"E198.MirrorCS"),sQuery(id+"F1.wireOp",EDGE,"E199"),sQuery(id+"F1.wireOp",EDGE,"E200"),sQuery(id+"F1.wireOp",EDGE,"E201"),sQuery(id+"F1.wireOp",EDGE,"E202")])],"isStart":false});
            extrude(context, id + "F11", {"entities" : qUnion([Q0]), "operationType" : NewBodyOperationType.ADD, "depth" : 44.45 * mm, "hasSecondDirection" : true, "secondDirectionOppositeDirection" : false, "secondDirectionBoundEntityFace" : qUnion([Q1]), "secondDirectionDepth" : 38.1 * mm});
        }
        {
            var Q0;
            Q0 = qSketchRegion(id + "F3", true);
            extrude(context, id + "F12", {"entities" : qUnion([Q0]), "operationType" : NewBodyOperationType.REMOVE, "endBound" : BoundingType.SYMMETRIC, "oppositeDirection" : true, "depth" : 30.86 * mm});
        }
        {
            var Q0;
            Q0=makeQuery(id+"F5.imprint","IMPRINT",FACE,{"disambiguationData":[TD([[makeQuery(id+"F5.imprint","IMPRINT",EDGE,{"derivedFrom":sQuery(id+"F5.wireOp",EDGE,"E268")}),1.0]])]});
            var Q1;
            Q1=makeQuery(id+"F5.imprint","IMPRINT",FACE,{"disambiguationData":[TD([[makeQuery(id+"F5.imprint","IMPRINT",EDGE,{"derivedFrom":sQuery(id+"F5.wireOp",EDGE,"E269")}),1.0]])]});
            var Q2;
            Q2=sQuery(id+"F5.wireOp",EDGE,"E269");
            var Q3;
            Q3=sQuery(id+"F5.wireOp",EDGE,"E268");
            extrude(context, id + "F13", {"entities" : qUnion([Q0, Q1]), "operationType" : NewBodyOperationType.REMOVE, "surfaceEntities" : qUnion([Q2, Q3]), "depth" : 7.11 * mm});
        }
        {
            var Q0;
            Q0=makeQuery(id+"F5.imprint","IMPRINT",FACE,{"disambiguationData":[TD([[makeQuery(id+"F5.imprint","IMPRINT",EDGE,{"derivedFrom":sQuery(id+"F5.wireOp",EDGE,"E267")}),1.0]])]});
            var Q1;
            Q1=sQuery(id+"F5.wireOp",EDGE,"E267");
            extrude(context, id + "F14", {"entities" : qUnion([Q0]), "operationType" : NewBodyOperationType.REMOVE, "surfaceEntities" : qUnion([Q1]), "depth" : 19.94 * mm});
        }
        {
            var Q0;
            {var subQ0=sQuery(id+"F6.wireOp",EDGE,"E273");Q0=makeQuery(id+"F6.imprint","IMPRINT",FACE,{"disambiguationData":[TD([[makeQuery(id+"F6.imprint","IMPRINT",EDGE,{"derivedFrom":subQ0}),1.0]])]});}
            var Q1;
            Q1=sQuery(id+"F6.wireOp",EDGE,"E274");
            revolve(context, id + "F15", {"operationType" : NewBodyOperationType.REMOVE, "entities" : qUnion([Q0]), "axis" : qUnion([Q1]), "revolveType" : RevolveType.FULL, "oppositeDirection" : true});
        }
        {
            var Q0;
            Q0 = qSketchRegion(id + "F7", true);
            extrude(context, id + "F16", {"entities" : qUnion([Q0]), "operationType" : NewBodyOperationType.REMOVE, "endBound" : BoundingType.SYMMETRIC, "oppositeDirection" : true, "depth" : 3.17 * mm});
        }
        {
            var Q0;
            Q0=makeQuery(id+"F11.opExtrude","SWEPT_EDGE",EDGE,{"disambiguationData":[OSD([sQuery(id+"F2.wireOp",EDGE,"E210.MirrorCS"),sQuery(id+"F2.wireOp",EDGE,"E211")])]});
            var Q1;
            Q1=makeQuery(id+"F11.opExtrude","SWEPT_EDGE",EDGE,{"disambiguationData":[OSD([sQuery(id+"F2.wireOp",EDGE,"E206"),sQuery(id+"F2.wireOp",EDGE,"E211")])]});
            var Q2;
            Q2=makeQuery(id+"F11.opExtrude","SWEPT_EDGE",EDGE,{"disambiguationData":[OSD([sQuery(id+"F2.wireOp",EDGE,"E209.MirrorCS"),sQuery(id+"F2.wireOp",EDGE,"E210.MirrorCS")])]});
            var Q3;
            Q3=makeQuery(id+"F11.opExtrude","SWEPT_EDGE",EDGE,{"disambiguationData":[OSD([sQuery(id+"F2.wireOp",EDGE,"E205"),sQuery(id+"F2.wireOp",EDGE,"E206")])]});
            fillet(context, id + "F17", {"entities" : qUnion([Q0, Q1, Q2, Q3]), "radius" : 5.08 * mm, "tangentPropagation" : true, "allowEdgeOverflow" : false});
        }
        {
            var Q0;
            {var subQ0=sQuery(id+"F2.wireOp",EDGE,"E210.MirrorCS");Q0=makeQuery(id+"F17.opFillet","BLEND_EDGE",EDGE,{"blendedFrom":[makeQuery(id+"F11.opExtrude","SWEPT_EDGE",EDGE,{"disambiguationData":[OSD([sQuery(id+"F2.wireOp",EDGE,"E209.MirrorCS"),subQ0])]}),makeQuery(id+"F11.opExtrude","SWEPT_EDGE",EDGE,{"disambiguationData":[OSD([subQ0,sQuery(id+"F2.wireOp",EDGE,"E211")])]})],"blendedInto":[]});}
            fillet(context, id + "F18", {"entities" : qUnion([Q0]), "radius" : 3.8 * mm, "tangentPropagation" : true, "allowEdgeOverflow" : false});
        }
        {
            var Q0;
            {var subQ0=sQuery(id+"F2.wireOp",EDGE,"E206");Q0=makeQuery(id+"F17.opFillet","BLEND_EDGE",EDGE,{"blendedFrom":[makeQuery(id+"F11.opExtrude","SWEPT_EDGE",EDGE,{"disambiguationData":[OSD([sQuery(id+"F2.wireOp",EDGE,"E205"),subQ0])]}),makeQuery(id+"F11.opExtrude","SWEPT_EDGE",EDGE,{"disambiguationData":[OSD([subQ0,sQuery(id+"F2.wireOp",EDGE,"E211")])]})],"blendedInto":[]});}
            fillet(context, id + "F19", {"entities" : qUnion([Q0]), "radius" : 3.8 * mm, "tangentPropagation" : true, "allowEdgeOverflow" : false});
        }
    });
